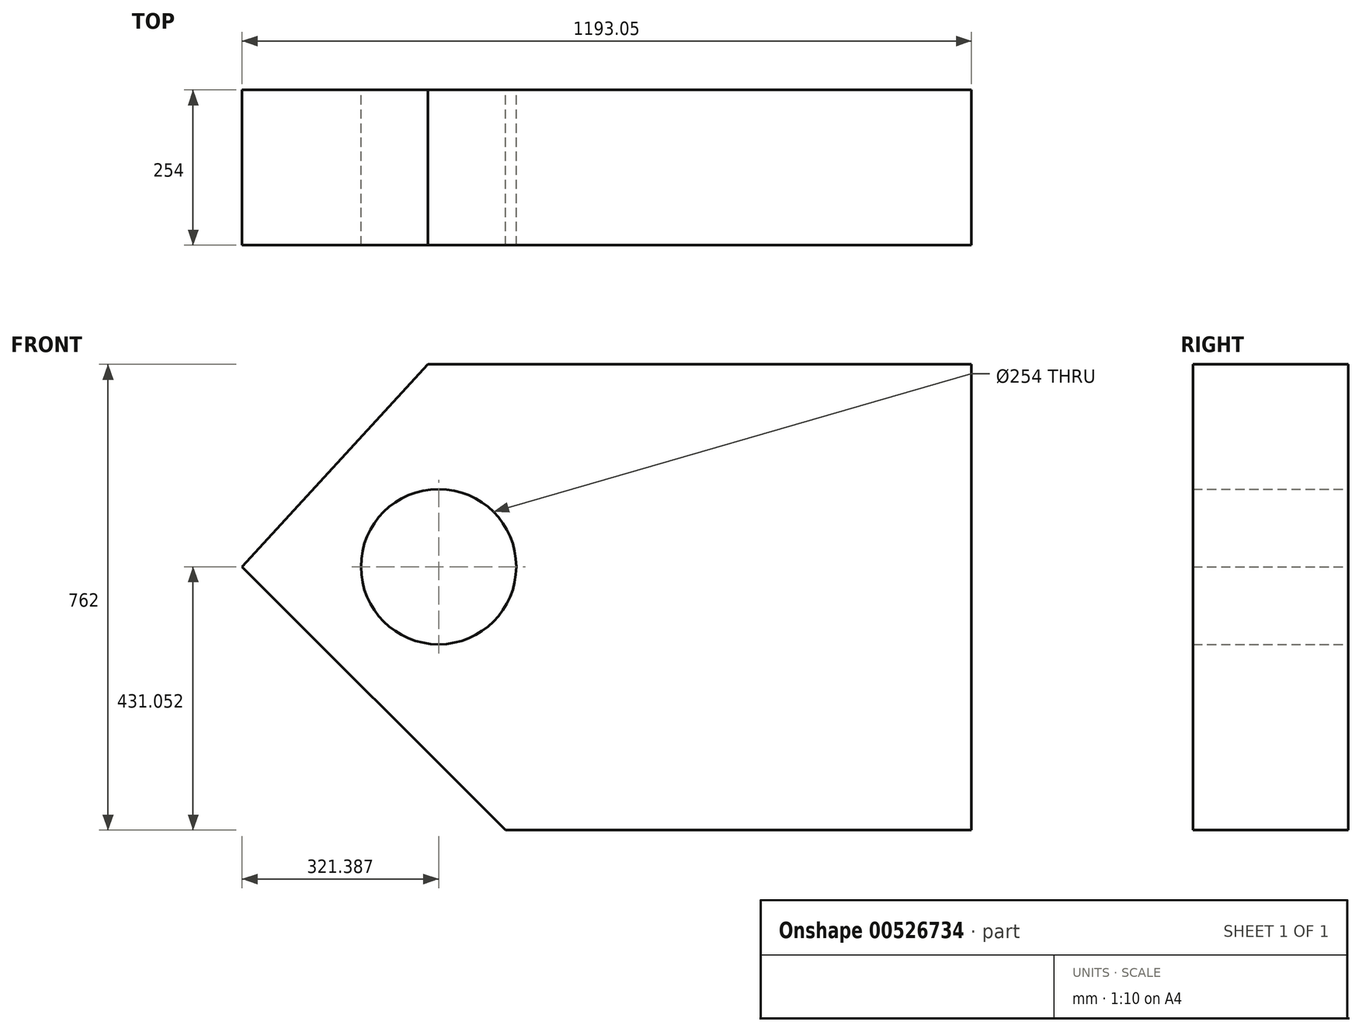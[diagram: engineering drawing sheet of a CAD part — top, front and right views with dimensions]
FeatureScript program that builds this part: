
annotation { "Feature Type Name" : "Feature", "Feature Type Description" : "" }
export const myFeature = defineFeature(function(context is Context, id is Id, definition is map)
    precondition{}
    {
        {
            var Q0;
            Q0=qCreatedBy(makeId("Front.planeOp"),FACE);
            var sketch = newSketch(context, id + "F0", { "sketchPlane" : qUnion([Q0])});
            skLineSegment(sketch, "E0", {"start": v(0, 0) * mm, "end": v(762, 0) * mm});
            skLineSegment(sketch, "E1", {"start": v(762, 0) * mm, "end": v(762, 762) * mm});
            skLineSegment(sketch, "E2", {"start": v(762, 762) * mm, "end": v(-127, 762) * mm});
            skLineSegment(sketch, "E3", {"start": v(0, 0) * mm, "end": v(-431.05, 431.05) * mm});
            skLineSegment(sketch, "E4", {"start": v(-431.05, 431.05) * mm, "end": v(-127, 762) * mm});
            skCircle(sketch, "E5", {"center": v(-109.66, 431.05) * mm, "radius": 127 * mm});
            skSolve(sketch);
        }
        {
            var Q0;
            Q0 = qSketchRegion(id + "F0", true);
            extrude(context, id + "F1", {"entities" : qUnion([Q0]), "depth" : 254 * mm, "offsetDistance" : 25.4 * mm});
        }
    });
